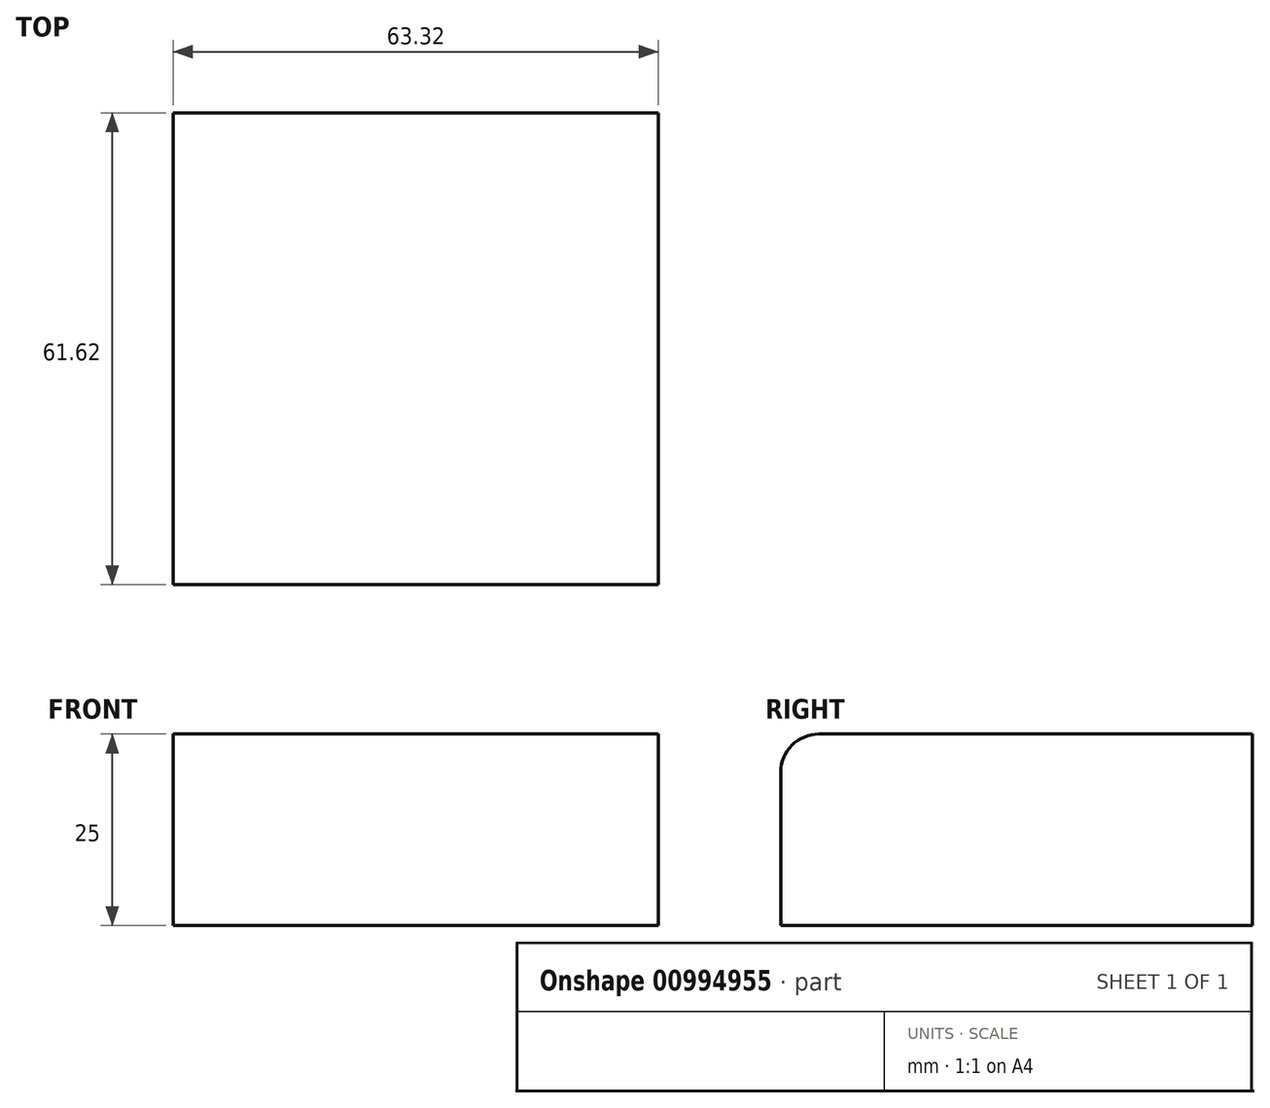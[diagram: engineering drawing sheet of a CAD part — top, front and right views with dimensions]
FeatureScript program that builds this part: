
annotation { "Feature Type Name" : "Feature", "Feature Type Description" : "" }
export const myFeature = defineFeature(function(context is Context, id is Id, definition is map)
    precondition{}
    {
        {
            var Q0;
            Q0=qCreatedBy(makeId("Top.planeOp"),FACE);
            var sketch = newSketch(context, id + "F0", { "sketchPlane" : qUnion([Q0])});
            skLineSegment(sketch, "E0.bottom", {"start": v(31.66, -30.8) * mm, "end": v(-31.66, -30.8) * mm});
            skLineSegment(sketch, "E0.top", {"start": v(31.66, 30.8) * mm, "end": v(-31.66, 30.8) * mm});
            skLineSegment(sketch, "E0.left", {"start": v(31.66, -30.8) * mm, "end": v(31.66, 30.8) * mm});
            skLineSegment(sketch, "E0.right", {"start": v(-31.66, -30.8) * mm, "end": v(-31.66, 30.8) * mm});
            skPoint(sketch, "E0.middle", {"position": v(0, 0) * mm});
            skSolve(sketch);
        }
        {
            var Q0;
            Q0 = qSketchRegion(id + "F0", true);
            extrude(context, id + "F1", {"entities" : qUnion([Q0]), "depth" : 25 * mm, "offsetDistance" : 25 * mm});
        }
        {
            var Q0;
            Q0=makeQuery(id+"F1.opExtrude","CAP_EDGE",EDGE,{"disambiguationData":[OSD([sQuery(id+"F0.wireOp",EDGE,"E0.bottom")])],"isStart":false});
            fillet(context, id + "F2", {"entities" : qUnion([Q0]), "radius" : 5 * mm, "tangentPropagation" : true, "allowEdgeOverflow" : false});
        }
    });
